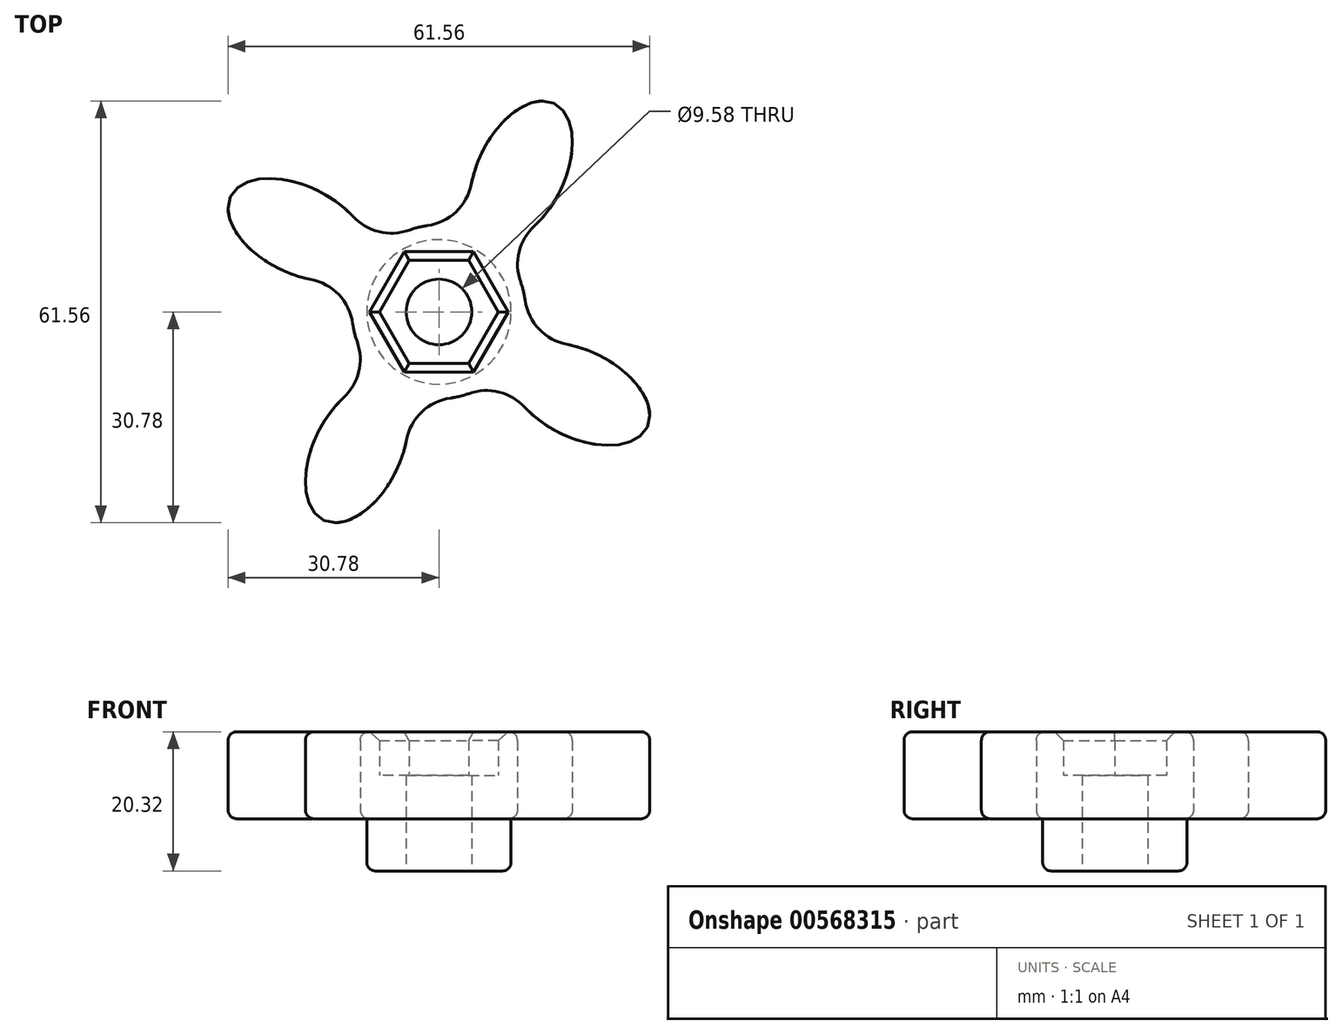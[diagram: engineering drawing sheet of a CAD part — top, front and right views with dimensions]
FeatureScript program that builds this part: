
annotation { "Feature Type Name" : "Feature", "Feature Type Description" : "" }
export const myFeature = defineFeature(function(context is Context, id is Id, definition is map)
    precondition{}
    {
        {
            var Q0;
            Q0=qCreatedBy(makeId("Top.planeOp"),FACE);
            var sketch = newSketch(context, id + "F0", { "sketchPlane" : qUnion([Q0])});
            skCircle(sketch, "E0.cCircle", {"center": v(0, 0) * mm, "radius": 7.52 * mm, "construction": true});
            skLineSegment(sketch, "E0.0", {"start": v(8.69, 0) * mm, "end": v(4.34, -7.52) * mm});
            skLineSegment(sketch, "E0.1", {"start": v(4.34, -7.52) * mm, "end": v(-4.34, -7.52) * mm});
            skLineSegment(sketch, "E0.2", {"start": v(-4.34, -7.52) * mm, "end": v(-8.69, 0) * mm});
            skLineSegment(sketch, "E0.3", {"start": v(-8.69, 0) * mm, "end": v(-4.34, 7.52) * mm});
            skLineSegment(sketch, "E0.4", {"start": v(-4.34, 7.52) * mm, "end": v(4.34, 7.52) * mm});
            skLineSegment(sketch, "E0.5", {"start": v(4.34, 7.52) * mm, "end": v(8.69, 0) * mm});
            skPoint(sketch, "E0.0.midPoint", {"position": v(6.52, -3.76) * mm});
            skArc(sketch, "E1", {"start": v(-12.58, -1.71) * mm, "mid": v(-12.33, -3.04) * mm, "end": v(-11.94, -4.34) * mm});
            skEllipticalArc(sketch, "E2", {});
            skArc(sketch, "E3", {"start": v(-12.58, -1.71) * mm, "mid": v(-14.6, 2.5) * mm, "end": v(-18.71, 4.75) * mm});
            skArc(sketch, "E4", {"start": v(-12.56, 13.95) * mm, "mid": v(-8.76, 11.7) * mm, "end": v(-4.34, 11.94) * mm});
            skArc(sketch, "E5.1.0", {"start": v(-13.95, -12.56) * mm, "mid": v(-11.7, -8.76) * mm, "end": v(-11.94, -4.34) * mm});
            skEllipticalArc(sketch, "E5.1.1", {});
            skArc(sketch, "E5.1.2", {"start": v(1.71, -12.58) * mm, "mid": v(-2.5, -14.6) * mm, "end": v(-4.75, -18.71) * mm});
            skArc(sketch, "E5.2.0", {"start": v(12.56, -13.95) * mm, "mid": v(8.76, -11.7) * mm, "end": v(4.34, -11.94) * mm});
            skEllipticalArc(sketch, "E5.2.1", {});
            skArc(sketch, "E5.2.2", {"start": v(12.58, 1.71) * mm, "mid": v(14.6, -2.5) * mm, "end": v(18.71, -4.75) * mm});
            skArc(sketch, "E5.3.0", {"start": v(13.95, 12.56) * mm, "mid": v(11.7, 8.76) * mm, "end": v(11.94, 4.34) * mm});
            skEllipticalArc(sketch, "E5.3.1", {});
            skArc(sketch, "E5.3.2", {"start": v(-1.71, 12.58) * mm, "mid": v(2.5, 14.6) * mm, "end": v(4.75, 18.71) * mm});
            skArc(sketch, "E6.trimOffspring", {"start": v(-1.71, 12.58) * mm, "mid": v(-3.04, 12.33) * mm, "end": v(-4.34, 11.94) * mm});
            skArc(sketch, "E7.trimOffspring", {"start": v(12.58, 1.71) * mm, "mid": v(12.33, 3.04) * mm, "end": v(11.94, 4.34) * mm});
            skArc(sketch, "E8.trimOffspring", {"start": v(1.71, -12.58) * mm, "mid": v(3.04, -12.33) * mm, "end": v(4.34, -11.94) * mm});
            const initialGuessF0  = {"E2": [-0.020467777985070455, 0.011987073942015935, 0.8979206845663937, -0.4401572948706167, 0.011049, 0.00635, 0.9716561350369776, 5.1581641121168165], "E5.1.1": [-0.011987073942015937, -0.020467777985070455, 0.4401572948706168, 0.8979206845663937, 0.011049, 0.00635, 0.9716561350369776, 5.1581641121168165], "E5.2.1": [0.020467777985070455, -0.011987073942015937, -0.8979206845663937, 0.44015729487061683, 0.011049, 0.00635, 0.9716561350369776, 5.1581641121168165], "E5.3.1": [0.011987073942015938, 0.020467777985070452, -0.4401572948706169, -0.8979206845663936, 0.011049, 0.00635, 0.9716561350369776, 5.1581641121168165]};
            skSetInitialGuess(sketch, initialGuessF0);
            skSolve(sketch);
        }
        {
            var Q0;
            Q0=makeQuery(id+"F0.imprint","IMPRINT",FACE,{"disambiguationData":[TD([[makeQuery(id+"F0.imprint","IMPRINT",EDGE,{"derivedFrom":sQuery(id+"F0.wireOp",EDGE,"E0.0")}),1.0]])]});
            extrude(context, id + "F1", {"entities" : qUnion([Q0]), "depth" : 12.7 * mm, "offsetDistance" : 25.4 * mm});
        }
        {
            var Q0;
            Q0=makeQuery(id+"F1.opExtrude","CAP_FACE",FACE,{"disambiguationData":[OSD([sQuery(id+"F0.wireOp",EDGE,"E0.0"),sQuery(id+"F0.wireOp",EDGE,"E0.1"),sQuery(id+"F0.wireOp",EDGE,"E0.2"),sQuery(id+"F0.wireOp",EDGE,"E0.3"),sQuery(id+"F0.wireOp",EDGE,"E0.4"),sQuery(id+"F0.wireOp",EDGE,"E0.5"),sQuery(id+"F0.wireOp",EDGE,"E1"),sQuery(id+"F0.wireOp",EDGE,"E2"),sQuery(id+"F0.wireOp",EDGE,"E3"),sQuery(id+"F0.wireOp",EDGE,"E4"),sQuery(id+"F0.wireOp",EDGE,"E5.1.0"),sQuery(id+"F0.wireOp",EDGE,"E5.1.1"),sQuery(id+"F0.wireOp",EDGE,"E5.1.2"),sQuery(id+"F0.wireOp",EDGE,"E5.2.0"),sQuery(id+"F0.wireOp",EDGE,"E5.2.1"),sQuery(id+"F0.wireOp",EDGE,"E5.2.2"),sQuery(id+"F0.wireOp",EDGE,"E5.3.0"),sQuery(id+"F0.wireOp",EDGE,"E5.3.1"),sQuery(id+"F0.wireOp",EDGE,"E5.3.2"),sQuery(id+"F0.wireOp",EDGE,"E6.trimOffspring"),sQuery(id+"F0.wireOp",EDGE,"E7.trimOffspring"),sQuery(id+"F0.wireOp",EDGE,"E8.trimOffspring")])],"isStart":true});
            var sketch = newSketch(context, id + "F2", { "sketchPlane" : qUnion([Q0])});
            skCircle(sketch, "E9", {"center": v(0, 0) * mm, "radius": 10.54 * mm});
            skSolve(sketch);
        }
        {
            var Q0;
            Q0 = qSketchRegion(id + "F2", true);
            extrude(context, id + "F3", {"entities" : qUnion([Q0]), "operationType" : NewBodyOperationType.ADD, "depth" : 7.62 * mm, "offsetDistance" : 25.4 * mm});
        }
        {
            var Q0;
            Q0=makeQuery(id+"F3.opExtrude","CAP_FACE",FACE,{"disambiguationData":[OSD([sQuery(id+"F2.wireOp",EDGE,"E9")])],"isStart":false});
            var sketch = newSketch(context, id + "F4", { "sketchPlane" : qUnion([Q0])});
            skCircle(sketch, "E10", {"center": v(0, 0) * mm, "radius": 4.79 * mm});
            skSolve(sketch);
        }
        {
            var Q0;
            Q0 = qSketchRegion(id + "F4", true);
            extrude(context, id + "F5", {"entities" : qUnion([Q0]), "operationType" : NewBodyOperationType.REMOVE, "oppositeDirection" : true, "depth" : 7.62 * mm, "offsetDistance" : 25.4 * mm});
        }
        {
            var Q0;
            Q0=makeQuery(id+"F3.opExtrude","CAP_FACE",FACE,{"disambiguationData":[OSD([sQuery(id+"F2.wireOp",EDGE,"E9")])],"isStart":true});
            var sketch = newSketch(context, id + "F6", { "sketchPlane" : qUnion([Q0])});
            skCircle(sketch, "E11.cCircle", {"center": v(0, 0) * mm, "radius": 7.52 * mm, "construction": true});
            skLineSegment(sketch, "E11.0", {"start": v(-4.34, 7.52) * mm, "end": v(4.34, 7.52) * mm});
            skLineSegment(sketch, "E11.1", {"start": v(4.34, 7.52) * mm, "end": v(8.69, 0) * mm});
            skLineSegment(sketch, "E11.2", {"start": v(8.69, 0) * mm, "end": v(4.34, -7.52) * mm});
            skLineSegment(sketch, "E11.3", {"start": v(4.34, -7.52) * mm, "end": v(-4.34, -7.52) * mm});
            skLineSegment(sketch, "E11.4", {"start": v(-4.34, -7.52) * mm, "end": v(-8.69, 0) * mm});
            skLineSegment(sketch, "E11.5", {"start": v(-8.69, 0) * mm, "end": v(-4.34, 7.52) * mm});
            skPoint(sketch, "E11.0.midPoint", {"position": v(0, 7.52) * mm});
            skSolve(sketch);
        }
        {
            var Q0;
            Q0=makeQuery(id+"F6.imprint","IMPRINT",FACE,{"disambiguationData":[TD([[makeQuery(id+"F6.imprint","IMPRINT",EDGE,{"derivedFrom":sQuery(id+"F6.wireOp",EDGE,"E11.0")}),-1.0]])]});
            extrude(context, id + "F7", {"entities" : qUnion([Q0]), "operationType" : NewBodyOperationType.ADD, "depth" : 6.35 * mm, "offsetDistance" : 25.4 * mm});
        }
        {
            var Q0;
            Q0=makeQuery(id+"F1.opExtrude","CAP_EDGE",EDGE,{"disambiguationData":[OSD([sQuery(id+"F0.wireOp",EDGE,"E5.3.1")])],"isStart":false});
            var Q1;
            Q1=makeQuery(id+"F1.opExtrude","CAP_EDGE",EDGE,{"disambiguationData":[OSD([sQuery(id+"F0.wireOp",EDGE,"E5.3.0")])],"isStart":false});
            var Q2;
            Q2=makeQuery(id+"F1.opExtrude","CAP_EDGE",EDGE,{"disambiguationData":[OSD([sQuery(id+"F0.wireOp",EDGE,"E5.2.2")])],"isStart":false});
            var Q3;
            Q3=makeQuery(id+"F1.opExtrude","CAP_EDGE",EDGE,{"disambiguationData":[OSD([sQuery(id+"F0.wireOp",EDGE,"E5.1.1")])],"isStart":true});
            var Q4;
            Q4=makeQuery(id+"F3.opExtrude","CAP_EDGE",EDGE,{"disambiguationData":[OSD([sQuery(id+"F2.wireOp",EDGE,"E9")])],"isStart":false});
            var Q5;
            Q5=makeQuery(id+"F5.boolean.opBoolean","COPY",EDGE,{"derivedFrom":makeQuery(id+"F5.opExtrude","CAP_EDGE",EDGE,{"disambiguationData":[OSD([sQuery(id+"F4.wireOp",EDGE,"E10")])],"isStart":true})});
            fillet(context, id + "F8", {"entities" : qUnion([Q0, Q1, Q2, Q3, Q4, Q5]), "radius" : 1.27 * mm, "tangentPropagation" : true, "allowEdgeOverflow" : false});
        }
        {
            var Q0;
            Q0=makeQuery(id+"F1.opExtrude","CAP_EDGE",EDGE,{"disambiguationData":[OSD([sQuery(id+"F0.wireOp",EDGE,"E0.1")])],"isStart":false});
            var Q1;
            Q1=makeQuery(id+"F1.opExtrude","CAP_EDGE",EDGE,{"disambiguationData":[OSD([sQuery(id+"F0.wireOp",EDGE,"E0.0")])],"isStart":false});
            var Q2;
            Q2=makeQuery(id+"F1.opExtrude","CAP_EDGE",EDGE,{"disambiguationData":[OSD([sQuery(id+"F0.wireOp",EDGE,"E0.5")])],"isStart":false});
            var Q3;
            Q3=makeQuery(id+"F1.opExtrude","CAP_EDGE",EDGE,{"disambiguationData":[OSD([sQuery(id+"F0.wireOp",EDGE,"E0.4")])],"isStart":false});
            var Q4;
            Q4=makeQuery(id+"F1.opExtrude","CAP_EDGE",EDGE,{"disambiguationData":[OSD([sQuery(id+"F0.wireOp",EDGE,"E0.3")])],"isStart":false});
            var Q5;
            Q5=makeQuery(id+"F1.opExtrude","CAP_EDGE",EDGE,{"disambiguationData":[OSD([sQuery(id+"F0.wireOp",EDGE,"E0.2")])],"isStart":false});
            chamfer(context, id + "F9", {"entities" : qUnion([Q0, Q1, Q2, Q3, Q4, Q5]), "width" : 1.27 * mm, "tangentPropagation" : true});
        }
    });
